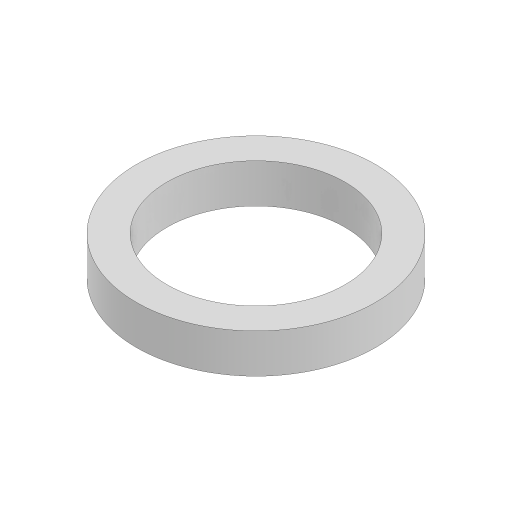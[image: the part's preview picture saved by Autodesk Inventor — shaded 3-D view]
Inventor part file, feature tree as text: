
AUTODESK INVENTOR PART (.ipt)
format: ipt  version: 2024 (Build 280153000, 153)  size: 98,304 bytes
history: native  units: in
note: dims shown in document units (in); Inventor stores cm internally (conversion verified against a paired STEP export)
features: extrude x1, direct_edit x1, sketch x1, other x1
ambient origin geometry x8: Origin, YZ Plane, XZ Plane, XY Plane, X Axis, Y Axis, Z Axis, Center Point
bodies: Solid1 (feature_tree)
feature tree (4):
  extrude  "Extrusion1"  Depth=0.25in
  direct_edit  "Direct Edit1"
  sketch  "Sketch1"  dims[d0=1.125in d1=0.2in d2=0.25in d3=0.0in d4=-0.005in]
  other  "Size1"
